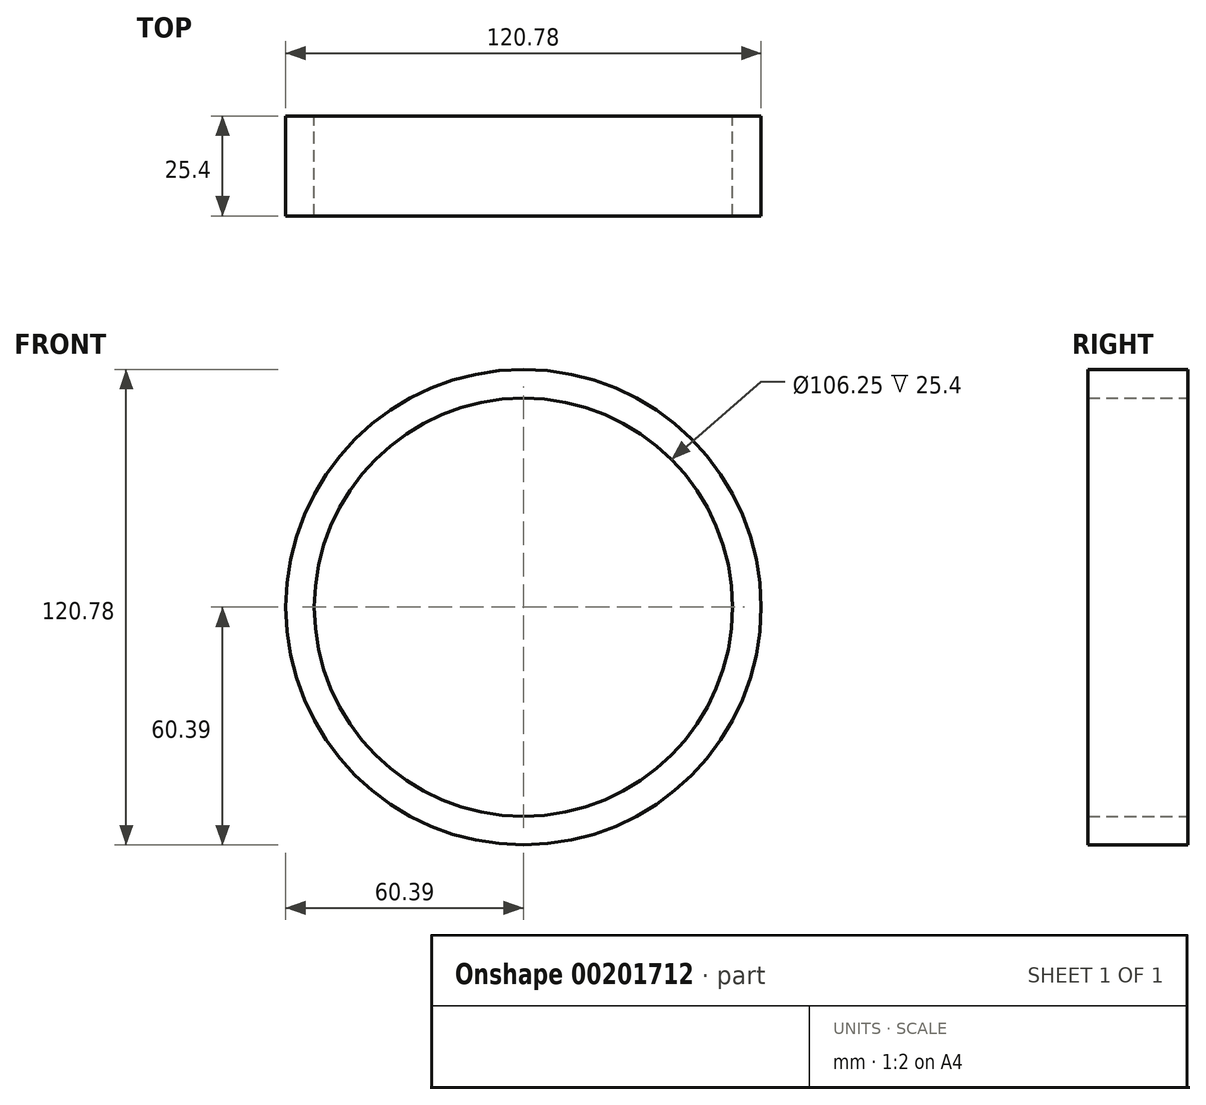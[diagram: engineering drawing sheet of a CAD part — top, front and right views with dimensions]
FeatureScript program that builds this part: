
annotation { "Feature Type Name" : "Feature", "Feature Type Description" : "" }
export const myFeature = defineFeature(function(context is Context, id is Id, definition is map)
    precondition{}
    {
        {
            var Q0;
            Q0=qCreatedBy(makeId("Front.planeOp"),FACE);
            var sketch = newSketch(context, id + "F0", { "sketchPlane" : qUnion([Q0])});
            skCircle(sketch, "E0", {"center": v(0, 0) * mm, "radius": 53.13 * mm});
            skCircle(sketch, "E1", {"center": v(0, 0) * mm, "radius": 60.4 * mm});
            skCircle(sketch, "E2", {"center": v(0, 0) * mm, "radius": 44.3 * mm});
            skCircle(sketch, "E3", {"center": v(0, 0) * mm, "radius": 35.6 * mm});
            skCircle(sketch, "E4", {"center": v(0, 0) * mm, "radius": 27.36 * mm});
            skCircle(sketch, "E5", {"center": v(0, 0) * mm, "radius": 19.28 * mm});
            skCircle(sketch, "E6", {"center": v(0, 0) * mm, "radius": 12.84 * mm});
            skCircle(sketch, "E7", {"center": v(0, 0) * mm, "radius": 6.83 * mm});
            skCircle(sketch, "E8", {"center": v(0, 0) * mm, "radius": 2.86 * mm});
            skSolve(sketch);
        }
        {
            var Q0;
            Q0=sQuery(id+"F0.wireOp",EDGE,"E1");
            var Q1;
            Q1=sQuery(id+"F0.wireOp",EDGE,"E0");
            var Q2;
            Q2=sQuery(id+"F0.wireOp",EDGE,"E2");
            var Q3;
            Q3=sQuery(id+"F0.wireOp",EDGE,"E3");
            var Q4;
            Q4=sQuery(id+"F0.wireOp",EDGE,"E4");
            var Q5;
            Q5=sQuery(id+"F0.wireOp",EDGE,"E5");
            var Q6;
            Q6=sQuery(id+"F0.wireOp",EDGE,"E6");
            var Q7;
            Q7=sQuery(id+"F0.wireOp",EDGE,"E7");
            var Q8;
            Q8=sQuery(id+"F0.wireOp",EDGE,"E8");
            extrude(context, id + "F1", {"bodyType" : ToolBodyType.SURFACE, "surfaceEntities" : qUnion([Q0, Q1, Q2, Q3, Q4, Q5, Q6, Q7, Q8]), "depth" : 25.4 * mm});
        }
        {
            var Q0;
            Q0 = qConstructionFilter(qBodyType(qCreatedBy(id + "F0" ,EDGE), BodyType.WIRE), ConstructionObject.NO);
            extrude(context, id + "F2", {"bodyType" : ToolBodyType.SURFACE, "surfaceEntities" : qUnion([Q0]), "depth" : 25.4 * mm});
        }
        {
            var Q0;
            Q0 = qSketchRegion(id + "F0", true);
            extrude(context, id + "F3", {"entities" : qUnion([Q0]), "depth" : 25.4 * mm});
        }
        {
            var Q0;
            Q0 = qSketchRegion(id + "F0", true);
            extrude(context, id + "F4", {"entities" : qUnion([Q0]), "operationType" : NewBodyOperationType.ADD, "depth" : 25.4 * mm});
        }
    });
